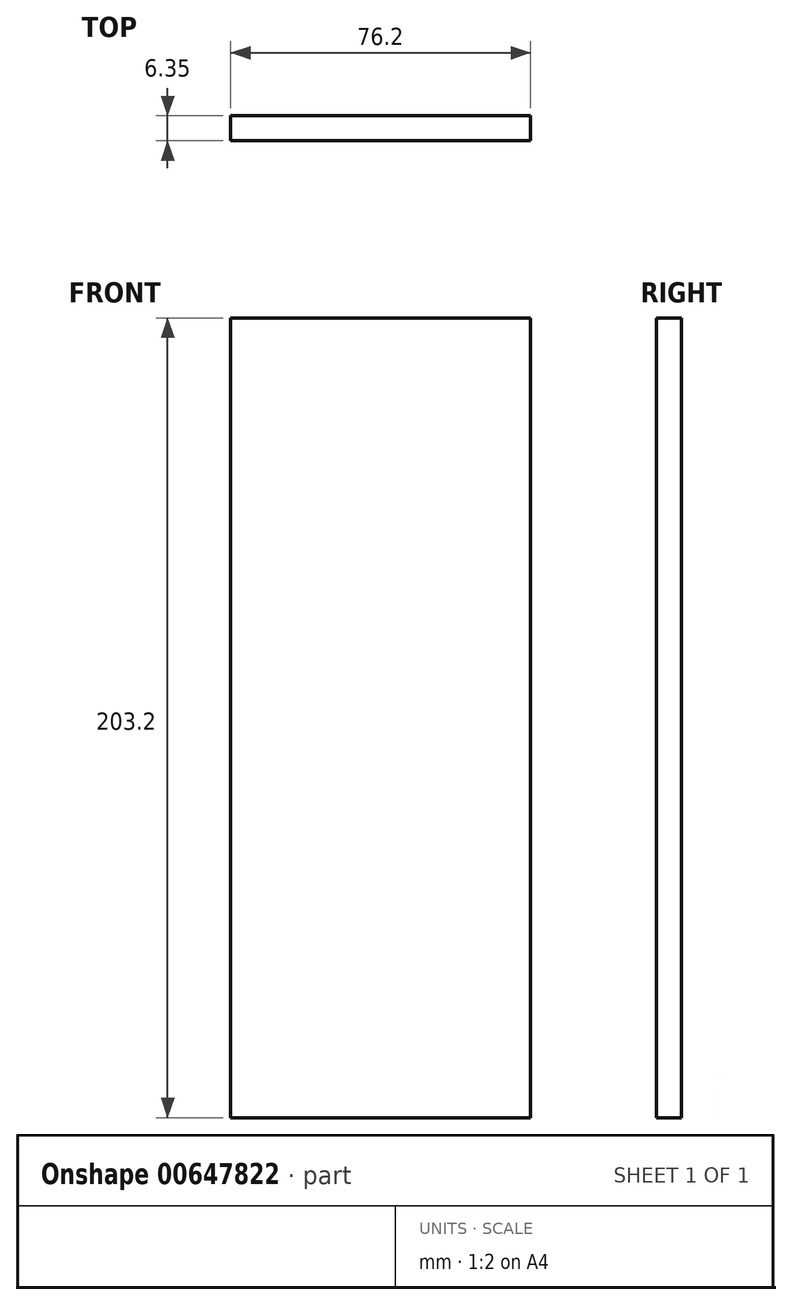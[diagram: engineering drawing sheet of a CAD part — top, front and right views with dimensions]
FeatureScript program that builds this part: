
annotation { "Feature Type Name" : "Feature", "Feature Type Description" : "" }
export const myFeature = defineFeature(function(context is Context, id is Id, definition is map)
    precondition{}
    {
        {
            var Q0;
            Q0=qCreatedBy(makeId("Front.planeOp"),FACE);
            var sketch = newSketch(context, id + "F0", { "sketchPlane" : qUnion([Q0])});
            skLineSegment(sketch, "E0.bottom", {"start": v(38.1, 101.6) * mm, "end": v(-38.1, 101.6) * mm});
            skLineSegment(sketch, "E0.top", {"start": v(38.1, -101.6) * mm, "end": v(-38.1, -101.6) * mm});
            skLineSegment(sketch, "E0.left", {"start": v(38.1, 101.6) * mm, "end": v(38.1, -101.6) * mm});
            skLineSegment(sketch, "E0.right", {"start": v(-38.1, 101.6) * mm, "end": v(-38.1, -101.6) * mm});
            skPoint(sketch, "E0.middle", {"position": v(0, 0) * mm});
            skSolve(sketch);
        }
        {
            var Q0;
            Q0=makeQuery(id+"F0.imprint","IMPRINT",FACE,{"disambiguationData":[TD([[makeQuery(id+"F0.imprint","IMPRINT",EDGE,{"derivedFrom":sQuery(id+"F0.wireOp",EDGE,"E0.bottom")}),1.0]])]});
            extrude(context, id + "F1", {"entities" : qUnion([Q0]), "depth" : 6.35 * mm, "offsetDistance" : 25.4 * mm});
        }
    });
